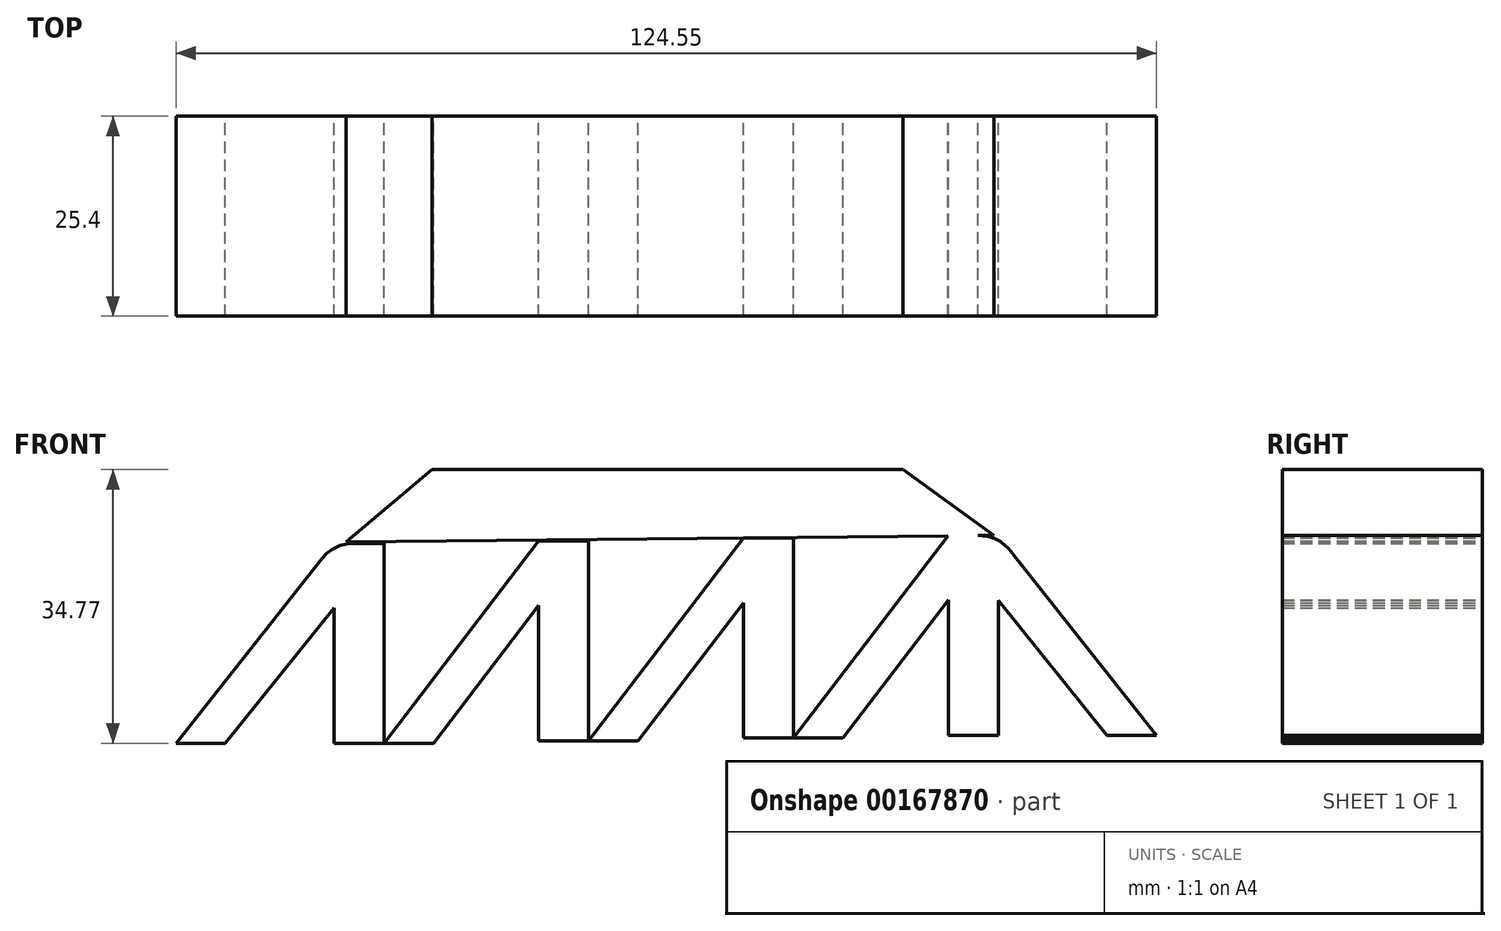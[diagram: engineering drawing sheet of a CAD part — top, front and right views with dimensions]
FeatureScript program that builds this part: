
annotation { "Feature Type Name" : "Feature", "Feature Type Description" : "" }
export const myFeature = defineFeature(function(context is Context, id is Id, definition is map)
    precondition{}
    {
        {
            var Q0;
            Q0=qCreatedBy(makeId("Front.planeOp"),FACE);
            var sketch = newSketch(context, id + "F0", { "sketchPlane" : qUnion([Q0])});
            skLineSegment(sketch, "E0.bottom", {"start": v(-62.18, -56.1) * mm, "end": v(-68.53, -56.1) * mm});
            skLineSegment(sketch, "E0.top", {"start": v(-62.18, -30.7) * mm, "end": v(-68.53, -30.7) * mm});
            skLineSegment(sketch, "E0.left", {"start": v(-62.18, -56.1) * mm, "end": v(-62.18, -30.7) * mm});
            skLineSegment(sketch, "E0.right", {"start": v(-68.53, -56.1) * mm, "end": v(-68.53, -30.7) * mm});
            skLineSegment(sketch, "E1.bottom", {"start": v(-42.52, -55.76) * mm, "end": v(-36.17, -55.76) * mm});
            skLineSegment(sketch, "E1.top", {"start": v(-42.52, -30.36) * mm, "end": v(-36.17, -30.36) * mm});
            skLineSegment(sketch, "E1.left", {"start": v(-42.52, -55.76) * mm, "end": v(-42.52, -30.36) * mm});
            skLineSegment(sketch, "E1.right", {"start": v(-36.17, -55.76) * mm, "end": v(-36.17, -30.36) * mm});
            skLineSegment(sketch, "E2", {"start": v(-42.52, -30.36) * mm, "end": v(-62.18, -56.1) * mm});
            skLineSegment(sketch, "E3", {"start": v(-62.18, -56.1) * mm, "end": v(-55.9, -56.1) * mm});
            skLineSegment(sketch, "E4", {"start": v(-55.9, -56.1) * mm, "end": v(-42.52, -38.58) * mm});
            skLineSegment(sketch, "E5", {"start": v(-42.52, -38.58) * mm, "end": v(-42.52, -30.36) * mm});
            skLineSegment(sketch, "E6.bottom", {"start": v(-10.16, -55.43) * mm, "end": v(-16.51, -55.43) * mm});
            skLineSegment(sketch, "E6.top", {"start": v(-10.16, -30.03) * mm, "end": v(-16.51, -30.03) * mm});
            skLineSegment(sketch, "E6.left", {"start": v(-10.16, -55.43) * mm, "end": v(-10.16, -30.03) * mm});
            skLineSegment(sketch, "E6.right", {"start": v(-16.51, -55.43) * mm, "end": v(-16.51, -30.03) * mm});
            skLineSegment(sketch, "E7.bottom", {"start": v(9.5, -55.1) * mm, "end": v(15.85, -55.1) * mm});
            skLineSegment(sketch, "E7.top", {"start": v(9.5, -29.7) * mm, "end": v(15.85, -29.7) * mm});
            skLineSegment(sketch, "E7.left", {"start": v(9.5, -55.1) * mm, "end": v(9.5, -29.7) * mm});
            skLineSegment(sketch, "E7.right", {"start": v(15.85, -55.1) * mm, "end": v(15.85, -29.7) * mm});
            skLineSegment(sketch, "E8", {"start": v(9.5, -29.7) * mm, "end": v(-10.16, -55.43) * mm});
            skLineSegment(sketch, "E9", {"start": v(-10.16, -55.43) * mm, "end": v(-3.89, -55.43) * mm});
            skLineSegment(sketch, "E10", {"start": v(-3.89, -55.43) * mm, "end": v(9.5, -37.92) * mm});
            skLineSegment(sketch, "E11", {"start": v(9.5, -37.92) * mm, "end": v(9.5, -29.7) * mm});
            skLineSegment(sketch, "E12", {"start": v(-16.51, -35.31) * mm, "end": v(-16.51, -30.03) * mm});
            skLineSegment(sketch, "E13", {"start": v(-16.51, -30.03) * mm, "end": v(-36.17, -55.76) * mm});
            skLineSegment(sketch, "E14", {"start": v(-29.9, -55.76) * mm, "end": v(-16.51, -38.25) * mm});
            skLineSegment(sketch, "E15", {"start": v(-16.51, -38.25) * mm, "end": v(-16.51, -30.03) * mm});
            skLineSegment(sketch, "E16", {"start": v(-29.9, -55.76) * mm, "end": v(-36.17, -55.76) * mm});
            skLineSegment(sketch, "E17", {"start": v(15.85, -29.7) * mm, "end": v(35.93, -55.1) * mm});
            skLineSegment(sketch, "E18", {"start": v(35.93, -55.1) * mm, "end": v(29.66, -55.1) * mm});
            skLineSegment(sketch, "E19", {"start": v(29.66, -55.1) * mm, "end": v(15.85, -37.92) * mm});
            skLineSegment(sketch, "E20", {"start": v(-68.53, -30.7) * mm, "end": v(-88.62, -56.1) * mm});
            skLineSegment(sketch, "E21", {"start": v(-88.62, -56.1) * mm, "end": v(-82.34, -56.1) * mm});
            skLineSegment(sketch, "E22", {"start": v(-82.34, -56.1) * mm, "end": v(-68.53, -38.91) * mm});
            skSolve(sketch);
        }
        {
            var Q0;
            Q0=makeQuery(id+"F0.imprint","IMPRINT",FACE,{"disambiguationData":[TD([[makeQuery(id+"F0.imprint","IMPRINT",EDGE,{"derivedFrom":sQuery(id+"F0.wireOp",EDGE,"E8")}),1.0]])]});
            var Q1;
            {var subQ1=sQuery(id+"F0.wireOp",EDGE,"E0.bottom");Q1=makeQuery(id+"F0.imprint","IMPRINT",FACE,{"disambiguationData":[TD([[makeQuery(id+"F0.imprint","IMPRINT",EDGE,{"derivedFrom":subQ1}),-1.0]])]});}
            var Q2;
            {var subQ0=sQuery(id+"F0.wireOp",EDGE,"E17");Q2=makeQuery(id+"F0.imprint","IMPRINT",FACE,{"disambiguationData":[TD([[makeQuery(id+"F0.imprint","IMPRINT",EDGE,{"derivedFrom":subQ0}),-1.0]])]});}
            var Q3;
            {var subQ1=sQuery(id+"F0.wireOp",EDGE,"E13");Q3=makeQuery(id+"F0.imprint","IMPRINT",FACE,{"disambiguationData":[TD([[makeQuery(id+"F0.imprint","IMPRINT",EDGE,{"derivedFrom":subQ1}),1.0]])]});}
            var Q4;
            Q4=makeQuery(id+"F0.imprint","IMPRINT",FACE,{"disambiguationData":[TD([[makeQuery(id+"F0.imprint","IMPRINT",EDGE,{"derivedFrom":sQuery(id+"F0.wireOp",EDGE,"E2")}),1.0]])]});
            var Q5;
            Q5=makeQuery(id+"F0.imprint","IMPRINT",FACE,{"disambiguationData":[TD([[makeQuery(id+"F0.imprint","IMPRINT",EDGE,{"derivedFrom":sQuery(id+"F0.wireOp",EDGE,"E6.bottom")}),-1.0]])]});
            var Q6;
            {var subQ0=sQuery(id+"F0.wireOp",EDGE,"E20");Q6=makeQuery(id+"F0.imprint","IMPRINT",FACE,{"disambiguationData":[TD([[makeQuery(id+"F0.imprint","IMPRINT",EDGE,{"derivedFrom":subQ0}),1.0]])]});}
            var Q7;
            Q7=makeQuery(id+"F0.imprint","IMPRINT",FACE,{"disambiguationData":[TD([[makeQuery(id+"F0.imprint","IMPRINT",EDGE,{"derivedFrom":sQuery(id+"F0.wireOp",EDGE,"E1.bottom")}),1.0]])]});
            var Q8;
            {var subQ1=sQuery(id+"F0.wireOp",EDGE,"E7.bottom");Q8=makeQuery(id+"F0.imprint","IMPRINT",FACE,{"disambiguationData":[TD([[makeQuery(id+"F0.imprint","IMPRINT",EDGE,{"derivedFrom":subQ1}),1.0]])]});}
            extrude(context, id + "F1", {"entities" : qUnion([Q0, Q1, Q2, Q3, Q4, Q5, Q6, Q7, Q8]), "depth" : 25.4 * mm});
        }
        {
            var Q0;
            Q0=makeQuery(id+"F1.opExtrude","SWEPT_EDGE",EDGE,{"disambiguationData":[OSD([sQuery(id+"F0.wireOp",EDGE,"E0.top"),sQuery(id+"F0.wireOp",EDGE,"E0.right"),sQuery(id+"F0.wireOp",EDGE,"E20")])]});
            fillet(context, id + "F2", {"entities" : qUnion([Q0]), "radius" : 5.08 * mm, "tangentPropagation" : true, "allowEdgeOverflow" : false});
        }
        {
            var Q0;
            Q0=makeQuery(id+"F1.opExtrude","SWEPT_EDGE",EDGE,{"disambiguationData":[OSD([sQuery(id+"F0.wireOp",EDGE,"E7.top"),sQuery(id+"F0.wireOp",EDGE,"E7.right"),sQuery(id+"F0.wireOp",EDGE,"E17")])]});
            fillet(context, id + "F3", {"entities" : qUnion([Q0]), "radius" : 5.08 * mm, "tangentPropagation" : true, "allowEdgeOverflow" : false});
        }
        {
            var Q0;
            Q0=qCreatedBy(makeId("Front.planeOp"),FACE);
            var sketch = newSketch(context, id + "F4", { "sketchPlane" : qUnion([Q0])});
            skLineSegment(sketch, "E23", {"start": v(-66.98, -30.52) * mm, "end": v(-56.06, -21.33) * mm});
            skLineSegment(sketch, "E24", {"start": v(15.3, -29.68) * mm, "end": v(-66.98, -30.52) * mm});
            skLineSegment(sketch, "E25", {"start": v(15.3, -29.68) * mm, "end": v(3.72, -21.33) * mm});
            skLineSegment(sketch, "E26", {"start": v(3.72, -21.33) * mm, "end": v(-56.06, -21.33) * mm});
            skSolve(sketch);
        }
        {
            var Q0;
            Q0=makeQuery(id+"F4.imprint","IMPRINT",FACE,{"disambiguationData":[TD([[makeQuery(id+"F4.imprint","IMPRINT",EDGE,{"derivedFrom":sQuery(id+"F4.wireOp",EDGE,"E23")}),-1.0]])]});
            extrude(context, id + "F5", {"entities" : qUnion([Q0]), "operationType" : NewBodyOperationType.ADD, "depth" : 25.4 * mm});
        }
    });
